# Revit family: Haworth_Planes_ConferenceTable_RectangularThreePiece
name_source: partatom
category: Furniture Systems
revit_build: Autodesk Revit 2018 (Build: 20170223_1515(x64)
units: mm (PartAtom-declared; Revit-internal decimal feet)

## family parameters
Always vertical = Yes
Cut with Voids When Loaded = No
OmniClass Number = 23.40.70.14.64.21
OmniClass Title = Systems Furniture
Part Type = Normal
Room Calculation Point = No
Round Connector Dimension = Use Diameter
Shared = No
Work Plane-Based = No

## types (2) — shared parameters
Actual Depth = 60"
Actual Height = 29"
Actual Knife Edge = No
Actual Width = 270"
Assembly Code = E2020200
Cable Base = Yes
Center Cutout Offset = 45"
Center Leg_Interior = No
Center Leg_Perimeter = No
Custom Size = No
Cutout = Yes
Cutout Depth = 4"
Cutout Width = 8"
Depth = 60"
Edgeband = Yes
Knife Edge = No
Manufacturer = Haworth
Max. Depth = 60"
Max. Height = 29"
Max. Width = 270"
Min. Depth = 42"
Min. Height = 29"
Min. Width = 186"
Min/Max Width = 186-270 @ 6 in. increments
Model = TARA
Not Cable Base = No
Opening Center = Yes
Opening Double = No
Opening Double Wide = No
Opening Left/Right = No
Opening Single = Yes
Opening Single Wide = No
Revision Number = 3
Side Cutout Offset = 22 1/2"
Standard Depths = 42, 48, 54, 60 in.
Standard Height = 29 in.
Support Height = 27 13/16"
Sustainability Info = https://www.haworth.com
Table Thickness = 1 3/16"
Third Width = 45"
URL = www.haworth.com
URL - Product = http://www.haworth.com
Warranty = http://www.haworth.com
Width = 270"

## per-type parameters (varying)
| type | Description | Interior Leg | Middle Leg_Interior | Middle Leg_Perimeter | Perimeter Leg | Side Middle Leg_Interior | Side Middle Leg_Perimeter | Support Location FrontBack | Support Location Side |
| 270w 60d - Interior Leg | Haworth - Planes Conference Table - Rectangular Three Piece - Interior Leg - 270w 60d | Yes | Yes | No | No | Yes | No | 3" | 3" |
| 270w 60d - Perimeter Leg | Haworth - Planes Conference Table - Rectangular Three Piece - Perimeter Leg - 270w 60d | No | No | Yes | Yes | No | Yes | 3/4" | 1 5/8" |

## geometry (parser evidence)
native form markers: Sweep x11
no freeform markers — native parametric forms only
